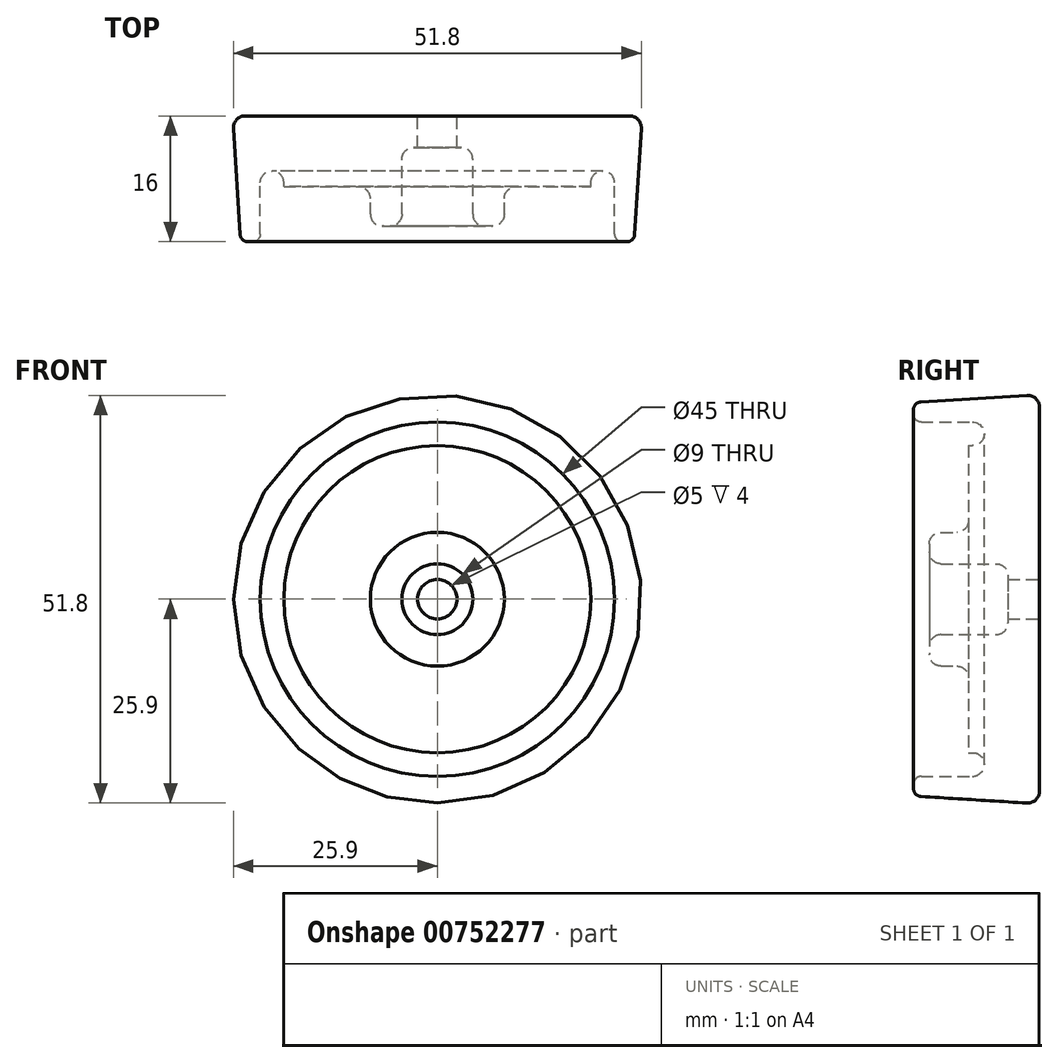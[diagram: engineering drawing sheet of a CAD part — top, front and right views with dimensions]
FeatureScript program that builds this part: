
annotation { "Feature Type Name" : "Feature", "Feature Type Description" : "" }
export const myFeature = defineFeature(function(context is Context, id is Id, definition is map)
    precondition{}
    {
        {
            var Q0;
            Q0=qCreatedBy(makeId("Right.planeOp"),FACE);
            var sketch = newSketch(context, id + "F0", { "sketchPlane" : qUnion([Q0])});
            skLineSegment(sketch, "E0", {"start": v(0, 0) * mm, "end": v(-4, 0) * mm});
            skLineSegment(sketch, "E1", {"start": v(-4, 0) * mm, "end": v(-4, 4.5) * mm});
            skLineSegment(sketch, "E2", {"start": v(-4, 4.5) * mm, "end": v(-14, 4.5) * mm});
            skLineSegment(sketch, "E3", {"start": v(-14, 4.5) * mm, "end": v(-14, 8.5) * mm});
            skLineSegment(sketch, "E4", {"start": v(-14, 8.5) * mm, "end": v(-9, 8.5) * mm});
            skLineSegment(sketch, "E5", {"start": v(-9, 8.5) * mm, "end": v(-9, 19.5) * mm});
            skLineSegment(sketch, "E6", {"start": v(-9, 19.5) * mm, "end": v(-7, 19.5) * mm});
            skLineSegment(sketch, "E7", {"start": v(-7, 19.5) * mm, "end": v(-7, 22.5) * mm});
            skLineSegment(sketch, "E8", {"start": v(-7, 22.5) * mm, "end": v(-16, 22.5) * mm});
            skLineSegment(sketch, "E9", {"start": v(-16, 22.5) * mm, "end": v(-16, 25) * mm});
            skLineSegment(sketch, "E10", {"start": v(-16, 25) * mm, "end": v(0, 26) * mm});
            skLineSegment(sketch, "E11", {"start": v(0, 26) * mm, "end": v(0, 0) * mm});
            skSolve(sketch);
        }
        {
            var Q0;
            Q0=makeQuery(id+"F0.imprint","IMPRINT",FACE,{"disambiguationData":[TD([[makeQuery(id+"F0.imprint","IMPRINT",EDGE,{"derivedFrom":sQuery(id+"F0.wireOp",EDGE,"E0")}),-1.0]])]});
            var Q1;
            Q1=sQuery(id+"F0.wireOp",EDGE,"E0");
            revolve(context, id + "F1", {"surfaceOperationType" : NewSurfaceOperationType.NEW, "entities" : qUnion([Q0]), "axis" : qUnion([Q1]), "revolveType" : RevolveType.FULL});
        }
        {
            var Q0;
            Q0=makeQuery(id+"F1.opRevolve","SWEPT_FACE",FACE,{"disambiguationData":[OSD([sQuery(id+"F0.wireOp",EDGE,"E11")])]});
            var sketch = newSketch(context, id + "F2", { "sketchPlane" : qUnion([Q0])});
            skPoint(sketch, "E12", {"position": v(0, 0) * mm});
            skSolve(sketch);
        }
        {
            var Q0;
            Q0=sQuery(id+"F2.wireOp",VERTEX,"E12");
            var Q1;
            Q1=makeQuery(id+"F1.opRevolve","SWEPT_BODY",BODY,{"disambiguationData":[OSD([sQuery(id+"F0.wireOp",EDGE,"E0"),sQuery(id+"F0.wireOp",EDGE,"E1"),sQuery(id+"F0.wireOp",EDGE,"E2"),sQuery(id+"F0.wireOp",EDGE,"E3"),sQuery(id+"F0.wireOp",EDGE,"E4"),sQuery(id+"F0.wireOp",EDGE,"E5"),sQuery(id+"F0.wireOp",EDGE,"E6"),sQuery(id+"F0.wireOp",EDGE,"E7"),sQuery(id+"F0.wireOp",EDGE,"E8"),sQuery(id+"F0.wireOp",EDGE,"E9"),sQuery(id+"F0.wireOp",EDGE,"E10"),sQuery(id+"F0.wireOp",EDGE,"E11")])]});
            hole(context, id + "F3", {"style" : HoleStyle.SIMPLE, "endStyle" : HoleEndStyle.THROUGH, "holeDiameter" : 5 * mm, "majorDiameter" : 5 * mm, "isTappedThrough" : true, "tappedDepth" : 12 * mm, "tapClearance" : 3, "locations" : qUnion([Q0]), "scope" : qUnion([Q1])});
        }
        {
            var Q0;
            Q0=makeQuery(id+"F1.opRevolve","SWEPT_EDGE",EDGE,{"disambiguationData":[OSD([sQuery(id+"F0.wireOp",EDGE,"E3"),sQuery(id+"F0.wireOp",EDGE,"E4")])]});
            var Q1;
            Q1=makeQuery(id+"F1.opRevolve","SWEPT_EDGE",EDGE,{"disambiguationData":[OSD([sQuery(id+"F0.wireOp",EDGE,"E2"),sQuery(id+"F0.wireOp",EDGE,"E3")])]});
            var Q2;
            Q2=makeQuery(id+"F1.opRevolve","SWEPT_EDGE",EDGE,{"disambiguationData":[OSD([sQuery(id+"F0.wireOp",EDGE,"E7"),sQuery(id+"F0.wireOp",EDGE,"E8")])]});
            var Q3;
            Q3=makeQuery(id+"F1.opRevolve","SWEPT_EDGE",EDGE,{"disambiguationData":[OSD([sQuery(id+"F0.wireOp",EDGE,"E6"),sQuery(id+"F0.wireOp",EDGE,"E7")])]});
            var Q4;
            Q4=makeQuery(id+"F3.hole-0.boolean.opBoolean","COPY",EDGE,{"derivedFrom":makeQuery(id+"F3.hole-0.opRevolve","SWEPT_EDGE",EDGE,{"disambiguationData":[OSD([sQuery(id+"F3.hole-0.sketch.wireOp",EDGE,"core_line_2"),sQuery(id+"F3.hole-0.sketch.wireOp",EDGE,"core_line_3")])]})});
            var Q5;
            Q5=makeQuery(id+"F1.opRevolve","SWEPT_EDGE",EDGE,{"disambiguationData":[OSD([sQuery(id+"F0.wireOp",EDGE,"E10"),sQuery(id+"F0.wireOp",EDGE,"E11")])]});
            var Q6;
            Q6=makeQuery(id+"F1.opRevolve","SWEPT_EDGE",EDGE,{"disambiguationData":[OSD([sQuery(id+"F0.wireOp",EDGE,"E1"),sQuery(id+"F0.wireOp",EDGE,"E2")])]});
            var Q7;
            Q7=makeQuery(id+"F1.opRevolve","SWEPT_EDGE",EDGE,{"disambiguationData":[OSD([sQuery(id+"F0.wireOp",EDGE,"E4"),sQuery(id+"F0.wireOp",EDGE,"E5")])]});
            fillet(context, id + "F4", {"entities" : qUnion([Q0, Q1, Q2, Q3, Q4, Q5, Q6, Q7]), "radius" : 1.5 * mm, "tangentPropagation" : true, "allowEdgeOverflow" : false});
        }
        {
            var Q0;
            Q0=makeQuery(id+"F1.opRevolve","SWEPT_EDGE",EDGE,{"disambiguationData":[OSD([sQuery(id+"F0.wireOp",EDGE,"E9"),sQuery(id+"F0.wireOp",EDGE,"E10")])]});
            var Q1;
            Q1=makeQuery(id+"F1.opRevolve","SWEPT_EDGE",EDGE,{"disambiguationData":[OSD([sQuery(id+"F0.wireOp",EDGE,"E8"),sQuery(id+"F0.wireOp",EDGE,"E9")])]});
            fillet(context, id + "F5", {"entities" : qUnion([Q0, Q1]), "radius" : 1 * mm, "tangentPropagation" : true, "allowEdgeOverflow" : false});
        }
    });
